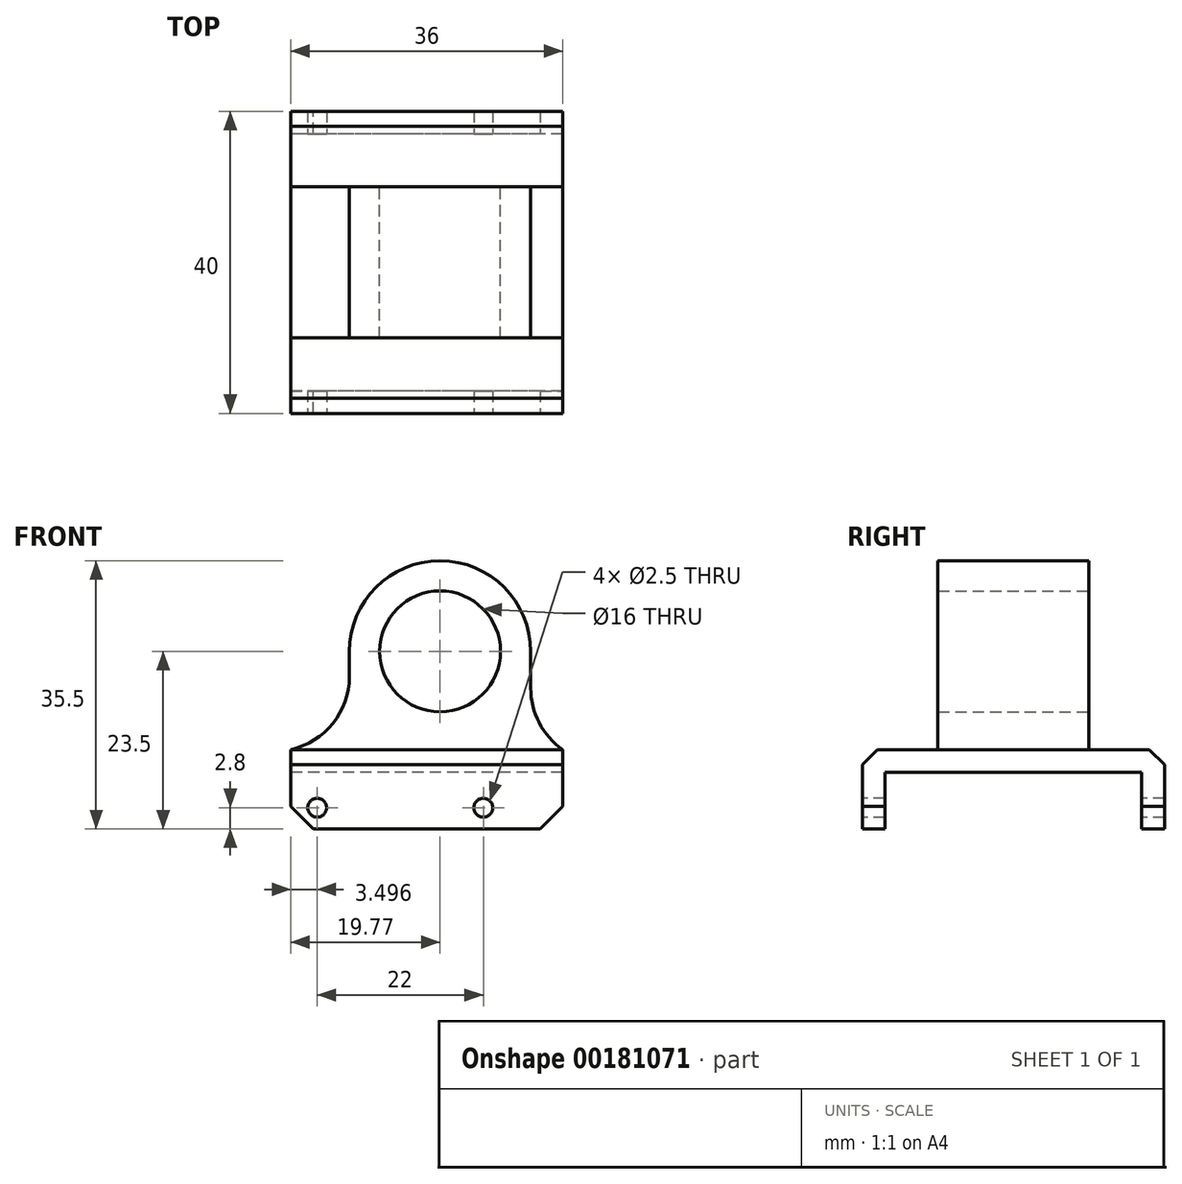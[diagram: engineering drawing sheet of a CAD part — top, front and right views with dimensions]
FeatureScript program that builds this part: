
annotation { "Feature Type Name" : "Feature", "Feature Type Description" : "" }
export const myFeature = defineFeature(function(context is Context, id is Id, definition is map)
    precondition{}
    {
        {
            var Q0;
            Q0=qCreatedBy(makeId("Front.planeOp"),FACE);
            var sketch = newSketch(context, id + "F0", { "sketchPlane" : qUnion([Q0])});
            skCircle(sketch, "E0", {"center": v(0, 0) * mm, "radius": 8 * mm});
            skArc(sketch, "E1", {"start": v(12, 0) * mm, "mid": v(0, 12) * mm, "end": v(-12, 0) * mm});
            skLineSegment(sketch, "E2", {"start": v(-12, 0) * mm, "end": v(12, 0) * mm});
            skLineSegment(sketch, "E3", {"start": v(-12, 0) * mm, "end": v(-12, -3.32) * mm});
            skLineSegment(sketch, "E4", {"start": v(12, 0) * mm, "end": v(12, -4.85) * mm});
            skArc(sketch, "E5", {"start": v(-19.77, -13) * mm, "mid": v(-14.18, -9.53) * mm, "end": v(-12, -3.32) * mm});
            skArc(sketch, "E6", {"start": v(12, -4.85) * mm, "mid": v(13.12, -9.44) * mm, "end": v(16.23, -13) * mm});
            skLineSegment(sketch, "E7", {"start": v(-19.77, -13) * mm, "end": v(16.23, -13) * mm});
            skLineSegment(sketch, "E8", {"start": v(-19.77, -13) * mm, "end": v(-19.77, -23.5) * mm});
            skLineSegment(sketch, "E9", {"start": v(-19.77, -23.5) * mm, "end": v(16.23, -23.5) * mm});
            skLineSegment(sketch, "E10", {"start": v(16.23, -23.5) * mm, "end": v(16.23, -13) * mm});
            skSolve(sketch);
        }
        {
            var Q0;
            Q0=makeQuery(id+"F0.imprint","IMPRINT",FACE,{"disambiguationData":[TD([[makeQuery(id+"F0.imprint","IMPRINT",EDGE,{"derivedFrom":sQuery(id+"F0.wireOp",EDGE,"E0")}),-1.0]])]});
            var Q1;
            {var subQ0=sQuery(id+"F0.wireOp",EDGE,"E3");Q1=makeQuery(id+"F0.imprint","IMPRINT",FACE,{"disambiguationData":[TD([[makeQuery(id+"F0.imprint","IMPRINT",EDGE,{"derivedFrom":subQ0}),1.0]])]});}
            extrude(context, id + "F1", {"entities" : qUnion([Q0, Q1]), "endBound" : BoundingType.SYMMETRIC, "depth" : 20 * mm});
        }
        {
            var Q0;
            Q0=makeQuery(id+"F0.imprint","IMPRINT",FACE,{"disambiguationData":[TD([[makeQuery(id+"F0.imprint","IMPRINT",EDGE,{"derivedFrom":sQuery(id+"F0.wireOp",EDGE,"E7")}),-1.0]])]});
            extrude(context, id + "F2", {"entities" : qUnion([Q0]), "operationType" : NewBodyOperationType.ADD, "endBound" : BoundingType.SYMMETRIC, "depth" : 40 * mm});
        }
        {
            var Q0;
            Q0=makeQuery(id+"F2.opExtrude","SWEPT_FACE",FACE,{"disambiguationData":[OSD([sQuery(id+"F0.wireOp",EDGE,"E8")])]});
            var sketch = newSketch(context, id + "F3", { "sketchPlane" : qUnion([Q0])});
            skLineSegment(sketch, "E11.bottom", {"start": v(-17, -23.5) * mm, "end": v(17, -23.5) * mm});
            skLineSegment(sketch, "E11.top", {"start": v(-17, -16) * mm, "end": v(17, -16) * mm});
            skLineSegment(sketch, "E11.left", {"start": v(-17, -23.5) * mm, "end": v(-17, -16) * mm});
            skLineSegment(sketch, "E11.right", {"start": v(17, -23.5) * mm, "end": v(17, -16) * mm});
            skSolve(sketch);
        }
        {
            var Q0;
            Q0=makeQuery(id+"F3.imprint","IMPRINT",FACE,{"disambiguationData":[TD([[makeQuery(id+"F3.imprint","IMPRINT",EDGE,{"derivedFrom":sQuery(id+"F3.wireOp",EDGE,"E11.bottom")}),-1.0]])]});
            extrude(context, id + "F4", {"entities" : qUnion([Q0]), "operationType" : NewBodyOperationType.REMOVE, "endBound" : BoundingType.THROUGH_ALL, "oppositeDirection" : true, "depth" : 25 * mm});
        }
        {
            var Q0;
            Q0=makeQuery(id+"F2.opExtrude","CAP_FACE",FACE,{"disambiguationData":[OSD([sQuery(id+"F0.wireOp",EDGE,"E7"),sQuery(id+"F0.wireOp",EDGE,"E8"),sQuery(id+"F0.wireOp",EDGE,"E9"),sQuery(id+"F0.wireOp",EDGE,"E10")])],"isStart":false});
            var sketch = newSketch(context, id + "F5", { "sketchPlane" : qUnion([Q0])});
            skCircle(sketch, "E12", {"center": v(-16.27, -20.7) * mm, "radius": 1.25 * mm});
            skCircle(sketch, "E13", {"center": v(5.73, -20.7) * mm, "radius": 1.25 * mm});
            skSolve(sketch);
        }
        {
            var Q0;
            Q0=makeQuery(id+"F5.imprint","IMPRINT",FACE,{"disambiguationData":[TD([[makeQuery(id+"F5.imprint","IMPRINT",EDGE,{"derivedFrom":sQuery(id+"F5.wireOp",EDGE,"E12")}),1.0]])]});
            var Q1;
            Q1=makeQuery(id+"F5.imprint","IMPRINT",FACE,{"disambiguationData":[TD([[makeQuery(id+"F5.imprint","IMPRINT",EDGE,{"derivedFrom":sQuery(id+"F5.wireOp",EDGE,"E13")}),1.0]])]});
            extrude(context, id + "F6", {"entities" : qUnion([Q0, Q1]), "operationType" : NewBodyOperationType.REMOVE, "oppositeDirection" : true, "depth" : 43.8 * mm});
        }
        {
            var Q0;
            {var subQ0=sQuery(id+"F0.wireOp",EDGE,"E9");var subQ1=sQuery(id+"F0.wireOp",EDGE,"E8");Q0=makeQuery(id+"F4.boolean.opBoolean","SPLIT",EDGE,{"disambiguationData":[TD([makeQuery(id+"F4.opExtrude","SWEPT_FACE",FACE,{"disambiguationData":[OSD([sQuery(id+"F3.wireOp",EDGE,"E11.right")])]})])],"derivedFrom":makeQuery(id+"F2.opExtrude","SWEPT_EDGE",EDGE,{"disambiguationData":[OSD([subQ1,subQ0])]})});}
            var Q1;
            {var subQ0=sQuery(id+"F0.wireOp",EDGE,"E9");var subQ1=sQuery(id+"F0.wireOp",EDGE,"E8");Q1=makeQuery(id+"F4.boolean.opBoolean","SPLIT",EDGE,{"disambiguationData":[TD([makeQuery(id+"F4.opExtrude","SWEPT_FACE",FACE,{"disambiguationData":[OSD([sQuery(id+"F3.wireOp",EDGE,"E11.left")])]})])],"derivedFrom":makeQuery(id+"F2.opExtrude","SWEPT_EDGE",EDGE,{"disambiguationData":[OSD([subQ1,subQ0])]})});}
            var Q2;
            {var subQ0=sQuery(id+"F0.wireOp",EDGE,"E10");var subQ1=sQuery(id+"F0.wireOp",EDGE,"E9");Q2=makeQuery(id+"F4.boolean.opBoolean","SPLIT",EDGE,{"disambiguationData":[TD([makeQuery(id+"F4.opExtrude","SWEPT_FACE",FACE,{"disambiguationData":[OSD([sQuery(id+"F3.wireOp",EDGE,"E11.left")])]})])],"derivedFrom":makeQuery(id+"F2.opExtrude","SWEPT_EDGE",EDGE,{"disambiguationData":[OSD([subQ1,subQ0])]})});}
            var Q3;
            {var subQ0=sQuery(id+"F0.wireOp",EDGE,"E10");var subQ1=sQuery(id+"F0.wireOp",EDGE,"E9");Q3=makeQuery(id+"F4.boolean.opBoolean","SPLIT",EDGE,{"disambiguationData":[TD([makeQuery(id+"F4.opExtrude","SWEPT_FACE",FACE,{"disambiguationData":[OSD([sQuery(id+"F3.wireOp",EDGE,"E11.right")])]})])],"derivedFrom":makeQuery(id+"F2.opExtrude","SWEPT_EDGE",EDGE,{"disambiguationData":[OSD([subQ1,subQ0])]})});}
            chamfer(context, id + "F7", {"entities" : qUnion([Q0, Q1, Q2, Q3]), "width" : 3 * mm, "tangentPropagation" : true});
        }
        {
            var Q0;
            Q0=makeQuery(id+"F2.opExtrude","CAP_EDGE",EDGE,{"disambiguationData":[OSD([sQuery(id+"F0.wireOp",EDGE,"E7")])],"isStart":false});
            var Q1;
            Q1=makeQuery(id+"F2.opExtrude","CAP_EDGE",EDGE,{"disambiguationData":[OSD([sQuery(id+"F0.wireOp",EDGE,"E7")])],"isStart":true});
            chamfer(context, id + "F8", {"entities" : qUnion([Q0, Q1]), "width" : 2 * mm, "tangentPropagation" : true});
        }
    });
